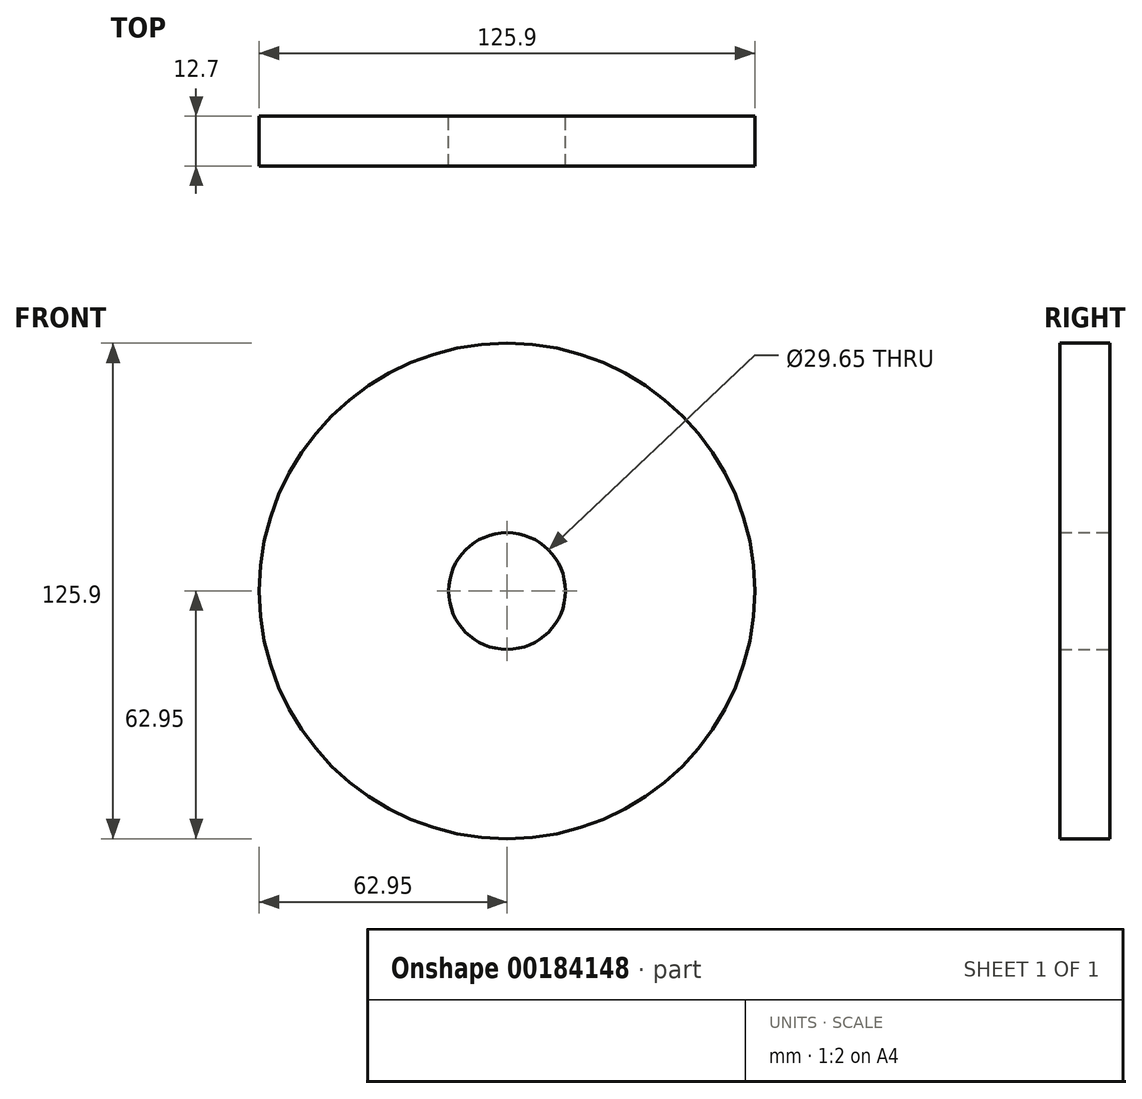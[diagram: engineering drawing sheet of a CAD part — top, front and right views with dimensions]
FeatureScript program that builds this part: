
annotation { "Feature Type Name" : "Feature", "Feature Type Description" : "" }
export const myFeature = defineFeature(function(context is Context, id is Id, definition is map)
    precondition{}
    {
        {
            var Q0;
            Q0=qCreatedBy(makeId("Front.planeOp"),FACE);
            var sketch = newSketch(context, id + "F0", { "sketchPlane" : qUnion([Q0])});
            skCircle(sketch, "E0", {"center": v(0, 0) * mm, "radius": 14.83 * mm});
            skCircle(sketch, "E1", {"center": v(0, 0) * mm, "radius": 62.95 * mm});
            skSolve(sketch);
        }
        {
            var Q0;
            Q0 = qSketchRegion(id + "F0", true);
            extrude(context, id + "F1", {"entities" : qUnion([Q0]), "depth" : 12.7 * mm});
        }
    });
